# Revit family: QF_COMCATER ALL BRANDS_RCT3-3G
name_source: partatom
category: Specialty Equipment
revit_build: Autodesk Revit 2014 (Build: 20140709_2115(x64)
units: mm (PartAtom-declared; Revit-internal decimal feet)

## types (2) — shared parameters
Accessory = No
Assembly Code = E1090320
BTUH = 3900 W
Depth Actual = 803 mm  [stored 2.63451 ft]
Description = GRIDDLE MODULAR TOP
Gas Flow = 0.0 L/s
Gas Size = 19 mm
Gas Size Flexible = 0 mm
Gas power kW = 3.9
Height Actual = 455 mm  [stored 1.49278 ft]
Length Actual = 300 mm
Manufacturer = TRUEHEAT
Model = RCT3-3G
Nominal Gas power = 3900 W
Type Comments = The Australian owned and designed* Trueheat RC Series of Gas Cooking Equipment has been developed for the restaurant and cafe market with a high quality finish, designed to fulfill the busy demands within a commercial kitchen.
16mm thick steel griddle plate with 16.5MJ/hr burner per 300mm section.
100% Flame failure controls included as standard. Piezo ignition on concealed burners.

## type names (no varying parameters)
- RCT3-3G_Natural Gas
- RCT3-3G_LPG

note: [stored X ft] marks values corroborated as IEEE doubles in the binary element streams (Revit-internal decimal feet)

## geometry (parser evidence)
native form markers: Sweep x5
no freeform markers — native parametric forms only
